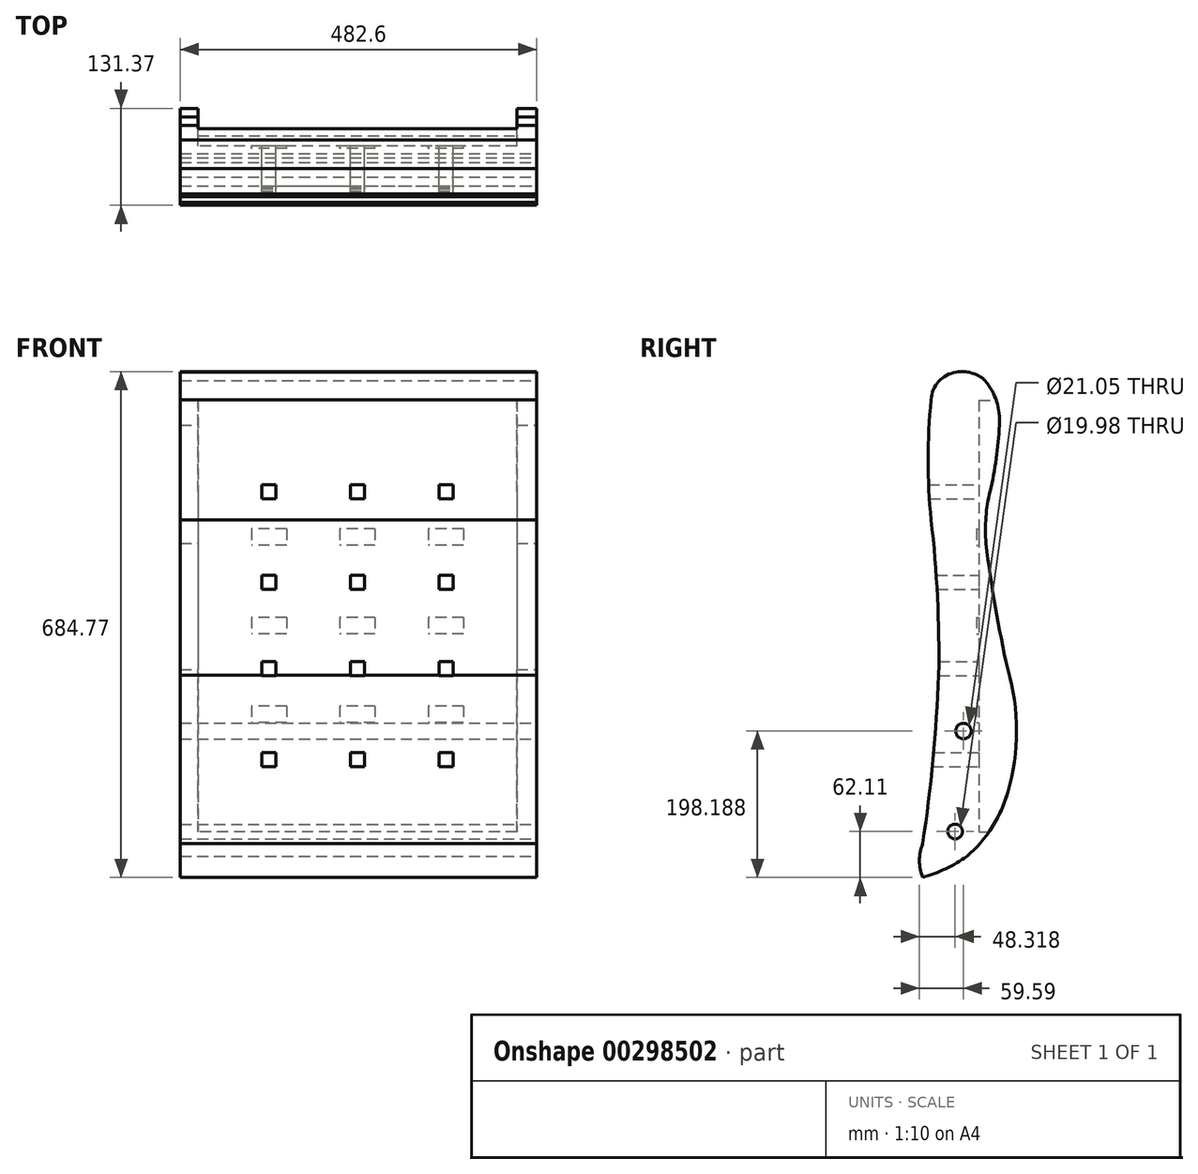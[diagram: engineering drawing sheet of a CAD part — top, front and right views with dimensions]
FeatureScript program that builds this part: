
annotation { "Feature Type Name" : "Feature", "Feature Type Description" : "" }
export const myFeature = defineFeature(function(context is Context, id is Id, definition is map)
    precondition{}
    {
        {
            var Q0;
            Q0=qCreatedBy(makeId("Front.planeOp"),FACE);
            var sketch = newSketch(context, id + "F0", { "sketchPlane" : qUnion([Q0])});
            skLineSegment(sketch, "E0.top", {"start": v(-241.3, -349.25) * mm, "end": v(241.3, -349.25) * mm});
            skLineSegment(sketch, "E0.left", {"start": v(-241.3, 323.85) * mm, "end": v(-241.3, -349.25) * mm});
            skLineSegment(sketch, "E0.right", {"start": v(241.3, 323.85) * mm, "end": v(241.3, -349.25) * mm});
            skPoint(sketch, "E1", {"position": v(0, 0) * mm});
            skPoint(sketch, "E1.positionSnap0", {"position": v(-241.3, 0) * mm});
            skPoint(sketch, "E1.positionSnap1", {"position": v(0, 349.25) * mm});
            skArc(sketch, "E2", {"start": v(241.3, 323.85) * mm, "mid": v(0, 349.25) * mm, "end": v(-241.3, 323.85) * mm});
            skPoint(sketch, "E3.orphan", {"position": v(-241.3, 349.25) * mm});
            skPoint(sketch, "E4.orphan", {"position": v(241.3, 349.25) * mm});
            skSolve(sketch);
        }
        {
            var Q0;
            Q0=makeQuery(id+"F0.imprint","IMPRINT",FACE,{"disambiguationData":[TD([[makeQuery(id+"F0.imprint","IMPRINT",EDGE,{"derivedFrom":sQuery(id+"F0.wireOp",EDGE,"E0.top")}),1.0]])]});
            extrude(context, id + "F1", {"entities" : qUnion([Q0]), "depth" : 120.65 * mm});
        }
        {
            var Q0;
            Q0=makeQuery(id+"F1.opExtrude","SWEPT_FACE",FACE,{"disambiguationData":[OSD([sQuery(id+"F0.wireOp",EDGE,"E0.left")])]});
            var sketch = newSketch(context, id + "F2", { "sketchPlane" : qUnion([Q0])});
            skArc(sketch, "E5", {"start": v(0, -233.65) * mm, "mid": v(21.35, -281.15) * mm, "end": v(55.28, -320.65) * mm});
            skArc(sketch, "E6", {"start": v(0, -68.14) * mm, "mid": v(-11.67, -150.9) * mm, "end": v(0, -233.65) * mm});
            skArc(sketch, "E7", {"start": v(0, -68.14) * mm, "mid": v(17, 17.17) * mm, "end": v(29.6, 103.23) * mm});
            skArc(sketch, "E8", {"start": v(29.6, 103.23) * mm, "mid": v(29.63, 138.4) * mm, "end": v(24.18, 173.15) * mm});
            skArc(sketch, "E9", {"start": v(11.41, 262.84) * mm, "mid": v(15.69, 217.7) * mm, "end": v(24.18, 173.15) * mm});
            skArc(sketch, "E10", {"start": v(30.93, 323.38) * mm, "mid": v(15.23, 295.03) * mm, "end": v(11.41, 262.84) * mm});
            skArc(sketch, "E11", {"start": v(69.98, 334.7) * mm, "mid": v(49.09, 333.77) * mm, "end": v(30.93, 323.38) * mm});
            skArc(sketch, "E12", {"start": v(103.92, 297.53) * mm, "mid": v(93.59, 322.17) * mm, "end": v(69.98, 334.7) * mm});
            skArc(sketch, "E13", {"start": v(103.92, 134.9) * mm, "mid": v(108, 216.21) * mm, "end": v(103.92, 297.53) * mm});
            skArc(sketch, "E14", {"start": v(103.92, 134.9) * mm, "mid": v(95.3, 29.96) * mm, "end": v(93.63, -75.3) * mm});
            skArc(sketch, "E15", {"start": v(93.63, -75.3) * mm, "mid": v(101.35, -189.73) * mm, "end": v(115.32, -303.56) * mm});
            skArc(sketch, "E16", {"start": v(115.32, -349.25) * mm, "mid": v(119.7, -326.4) * mm, "end": v(115.32, -303.56) * mm});
            skArc(sketch, "E17", {"start": v(55.28, -320.65) * mm, "mid": v(84.07, -337.54) * mm, "end": v(115.32, -349.25) * mm});
            skCircle(sketch, "E18", {"center": v(60.1, -151.06) * mm, "radius": 10.53 * mm});
            skCircle(sketch, "E19", {"center": v(71.38, -287.14) * mm, "radius": 9.99 * mm});
            skSolve(sketch);
        }
        {
            var Q0;
            {var subQ8=sQuery(id+"F2.wireOp",EDGE,"E5");Q0=makeQuery(id+"F2.imprint","IMPRINT",FACE,{"disambiguationData":[TD([[makeQuery(id+"F2.imprint","IMPRINT",EDGE,{"derivedFrom":subQ8}),1.0]])]});}
            var Q1;
            {var subQ0=sQuery(id+"F2.wireOp",EDGE,"E11");Q1=makeQuery(id+"F2.imprint","IMPRINT",FACE,{"disambiguationData":[TD([[makeQuery(id+"F2.imprint","IMPRINT",EDGE,{"derivedFrom":subQ0}),1.0]])]});}
            var Q2;
            {var subQ0=sQuery(id+"F2.wireOp",EDGE,"E6");Q2=makeQuery(id+"F2.imprint","IMPRINT",FACE,{"disambiguationData":[TD([[makeQuery(id+"F2.imprint","IMPRINT",EDGE,{"derivedFrom":subQ0}),1.0]])]});}
            extrude(context, id + "F3", {"entities" : qUnion([Q0, Q1, Q2]), "depth" : 482.6 * mm});
        }
        {
            var Q0;
            Q0=makeQuery(id+"F1.opExtrude","SWEPT_FACE",FACE,{"disambiguationData":[OSD([sQuery(id+"F0.wireOp",EDGE,"E0.right")])]});
            var sketch = newSketch(context, id + "F4", { "sketchPlane" : qUnion([Q0])});
            skLineSegment(sketch, "E20.bottom", {"start": v(-225.7, 393.7) * mm, "end": v(119.19, 393.7) * mm});
            skLineSegment(sketch, "E20.top", {"start": v(-225.7, -371) * mm, "end": v(119.19, -371) * mm});
            skLineSegment(sketch, "E20.left", {"start": v(-225.7, 393.7) * mm, "end": v(-225.7, -371) * mm});
            skLineSegment(sketch, "E20.right", {"start": v(119.19, 393.7) * mm, "end": v(119.19, -371) * mm});
            skSolve(sketch);
        }
        {
            var Q0;
            Q0=makeQuery(id+"F4.imprint","IMPRINT",FACE,{"disambiguationData":[TD([[makeQuery(id+"F4.imprint","IMPRINT",EDGE,{"derivedFrom":sQuery(id+"F4.wireOp",EDGE,"E20.bottom")}),-1.0]])]});
            var Q1;
            {var subQ0=sQuery(id+"F0.wireOp",EDGE,"E0.right");Q1=makeQuery(id+"F4.imprint","IMPRINT",FACE,{"disambiguationData":[TD([[makeQuery(id+"F4.imprint","IMPRINT",EDGE,{"derivedFrom":makeQuery(id+"F1.opExtrude","CAP_EDGE",EDGE,{"disambiguationData":[OSD([subQ0])],"isStart":true})}),-1.0]])]});}
            extrude(context, id + "F5", {"entities" : qUnion([Q0, Q1]), "operationType" : NewBodyOperationType.REMOVE, "oppositeDirection" : true, "depth" : 482.6 * mm});
        }
        {
            var Q0;
            Q0=makeQuery(id+"F3.opExtrude","CAP_EDGE",EDGE,{"disambiguationData":[OSD([sQuery(id+"F2.wireOp",EDGE,"E6")])],"isStart":false});
            cPoint(context, id + "F6", {"entities" : qUnion([Q0]), "parameter" : 0.5});
        }
        {
            var Q0;
            Q0=qCreatedBy(makeId("Front.planeOp"),FACE);
            var Q1;
            Q1 = qCreatedBy(id + "F6" ,VERTEX);
            cPlane(context, id + "F7", {"entities" : qUnion([Q0, Q1]), "cplaneType" : CPlaneType.PLANE_POINT, "offset" : 25.4 * mm, "width" : 152.4 * mm, "height" : 152.4 * mm});
        }
        {
            var Q0;
            Q0=qCreatedBy(id+"F7.planeOp",FACE);
            var sketch = newSketch(context, id + "F8", { "sketchPlane" : qUnion([Q0])});
            skLineSegment(sketch, "E21.bottom", {"start": v(-268.03, 296.48) * mm, "end": v(-699.83, 296.48) * mm});
            skLineSegment(sketch, "E21.top", {"start": v(-268.03, -287.72) * mm, "end": v(-699.83, -287.72) * mm});
            skLineSegment(sketch, "E21.left", {"start": v(-268.03, 296.48) * mm, "end": v(-268.03, -287.72) * mm});
            skLineSegment(sketch, "E21.right", {"start": v(-699.83, 296.48) * mm, "end": v(-699.83, -287.72) * mm});
            skPoint(sketch, "E22", {"position": v(-483.93, 296.48) * mm});
            skSolve(sketch);
        }
        {
            var Q0;
            Q0=makeQuery(id+"F8.imprint","IMPRINT",FACE,{"disambiguationData":[TD([[makeQuery(id+"F8.imprint","IMPRINT",EDGE,{"derivedFrom":sQuery(id+"F8.wireOp",EDGE,"E21.bottom")}),1.0]])]});
            extrude(context, id + "F9", {"entities" : qUnion([Q0]), "operationType" : NewBodyOperationType.REMOVE, "depth" : 50.8 * mm, "offsetDistance" : 25.4 * mm});
        }
        {
            var Q0;
            Q0=makeQuery(id+"F9.boolean.opBoolean","COPY",FACE,{"derivedFrom":makeQuery(id+"F9.opExtrude","CAP_FACE",FACE,{"disambiguationData":[OSD([sQuery(id+"F8.wireOp",EDGE,"E21.bottom"),sQuery(id+"F8.wireOp",EDGE,"E21.top"),sQuery(id+"F8.wireOp",EDGE,"E21.left"),sQuery(id+"F8.wireOp",EDGE,"E21.right")])],"isStart":false})});
            var sketch = newSketch(context, id + "F10", { "sketchPlane" : qUnion([Q0])});
            skLineSegment(sketch, "E23.bottom", {"start": v(340.26, -117.06) * mm, "end": v(387.89, -117.06) * mm});
            skLineSegment(sketch, "E23.top", {"start": v(340.26, -139.29) * mm, "end": v(387.89, -139.29) * mm});
            skLineSegment(sketch, "E23.left", {"start": v(340.26, -117.06) * mm, "end": v(340.26, -139.29) * mm});
            skLineSegment(sketch, "E23.right", {"start": v(387.89, -117.06) * mm, "end": v(387.89, -139.29) * mm});
            skLineSegment(sketch, "E24.bottom", {"start": v(579.98, 122.65) * mm, "end": v(627.6, 122.65) * mm});
            skLineSegment(sketch, "E24.top", {"start": v(579.98, 100.42) * mm, "end": v(627.6, 100.42) * mm});
            skLineSegment(sketch, "E24.left", {"start": v(579.98, 122.65) * mm, "end": v(579.98, 100.42) * mm});
            skLineSegment(sketch, "E24.right", {"start": v(627.6, 122.65) * mm, "end": v(627.6, 100.42) * mm});
            skLineSegment(sketch, "E25.bottom", {"start": v(340.26, 122.65) * mm, "end": v(387.89, 122.65) * mm});
            skLineSegment(sketch, "E25.top", {"start": v(340.26, 100.42) * mm, "end": v(387.89, 100.42) * mm});
            skLineSegment(sketch, "E25.left", {"start": v(340.26, 122.65) * mm, "end": v(340.26, 100.42) * mm});
            skLineSegment(sketch, "E25.right", {"start": v(387.89, 122.65) * mm, "end": v(387.89, 100.42) * mm});
            skLineSegment(sketch, "E26.bottom", {"start": v(460.12, 122.65) * mm, "end": v(507.75, 122.65) * mm});
            skLineSegment(sketch, "E26.top", {"start": v(460.12, 100.42) * mm, "end": v(507.75, 100.42) * mm});
            skLineSegment(sketch, "E26.left", {"start": v(460.12, 122.65) * mm, "end": v(460.12, 100.42) * mm});
            skLineSegment(sketch, "E26.right", {"start": v(507.75, 122.65) * mm, "end": v(507.75, 100.42) * mm});
            skLineSegment(sketch, "E27.bottom", {"start": v(460.12, 2.8) * mm, "end": v(507.75, 2.8) * mm});
            skLineSegment(sketch, "E27.top", {"start": v(460.12, -19.43) * mm, "end": v(507.75, -19.43) * mm});
            skLineSegment(sketch, "E27.left", {"start": v(460.12, 2.8) * mm, "end": v(460.12, -19.43) * mm});
            skLineSegment(sketch, "E27.right", {"start": v(507.75, 2.8) * mm, "end": v(507.75, -19.43) * mm});
            skLineSegment(sketch, "E28.bottom", {"start": v(579.98, 2.8) * mm, "end": v(627.6, 2.8) * mm});
            skLineSegment(sketch, "E28.top", {"start": v(579.98, -19.43) * mm, "end": v(627.6, -19.43) * mm});
            skLineSegment(sketch, "E28.left", {"start": v(579.98, 2.8) * mm, "end": v(579.98, -19.43) * mm});
            skLineSegment(sketch, "E28.right", {"start": v(627.6, 2.8) * mm, "end": v(627.6, -19.43) * mm});
            skLineSegment(sketch, "E29.bottom", {"start": v(340.26, 2.8) * mm, "end": v(387.89, 2.8) * mm});
            skLineSegment(sketch, "E29.top", {"start": v(340.26, -19.43) * mm, "end": v(387.89, -19.43) * mm});
            skLineSegment(sketch, "E29.left", {"start": v(340.26, 2.8) * mm, "end": v(340.26, -19.43) * mm});
            skLineSegment(sketch, "E29.right", {"start": v(387.89, 2.8) * mm, "end": v(387.89, -19.43) * mm});
            skLineSegment(sketch, "E30.bottom", {"start": v(579.98, -117.06) * mm, "end": v(627.6, -117.06) * mm});
            skLineSegment(sketch, "E30.top", {"start": v(579.98, -139.29) * mm, "end": v(627.6, -139.29) * mm});
            skLineSegment(sketch, "E30.left", {"start": v(579.98, -117.06) * mm, "end": v(579.98, -139.29) * mm});
            skLineSegment(sketch, "E30.right", {"start": v(627.6, -117.06) * mm, "end": v(627.6, -139.29) * mm});
            skLineSegment(sketch, "E31.bottom", {"start": v(460.12, -117.06) * mm, "end": v(507.75, -117.06) * mm});
            skLineSegment(sketch, "E31.top", {"start": v(460.12, -139.29) * mm, "end": v(507.75, -139.29) * mm});
            skLineSegment(sketch, "E31.left", {"start": v(460.12, -117.06) * mm, "end": v(460.12, -139.29) * mm});
            skLineSegment(sketch, "E31.right", {"start": v(507.75, -117.06) * mm, "end": v(507.75, -139.29) * mm});
            skLineSegment(sketch, "E32", {"start": v(268.03, 220.28) * mm, "end": v(699.83, 220.28) * mm});
            skLineSegment(sketch, "E33", {"start": v(268.03, -236.92) * mm, "end": v(699.83, -236.92) * mm});
            skLineSegment(sketch, "E34.bottom", {"start": v(474.4, -180.17) * mm, "end": v(493.46, -180.17) * mm});
            skLineSegment(sketch, "E34.top", {"start": v(474.4, -199.22) * mm, "end": v(493.46, -199.22) * mm});
            skLineSegment(sketch, "E34.left", {"start": v(474.4, -180.17) * mm, "end": v(474.4, -199.22) * mm});
            skLineSegment(sketch, "E34.right", {"start": v(493.46, -180.17) * mm, "end": v(493.46, -199.22) * mm});
            skLineSegment(sketch, "E35.bottom", {"start": v(474.4, -57.14) * mm, "end": v(493.46, -57.14) * mm});
            skLineSegment(sketch, "E35.top", {"start": v(474.4, -76.19) * mm, "end": v(493.46, -76.19) * mm});
            skLineSegment(sketch, "E35.left", {"start": v(474.4, -57.14) * mm, "end": v(474.4, -76.19) * mm});
            skLineSegment(sketch, "E35.right", {"start": v(493.46, -57.14) * mm, "end": v(493.46, -76.19) * mm});
            skLineSegment(sketch, "E36.bottom", {"start": v(594.26, -57.14) * mm, "end": v(613.31, -57.14) * mm});
            skLineSegment(sketch, "E36.top", {"start": v(594.26, -76.19) * mm, "end": v(613.31, -76.19) * mm});
            skLineSegment(sketch, "E36.left", {"start": v(594.26, -57.14) * mm, "end": v(594.26, -76.19) * mm});
            skLineSegment(sketch, "E36.right", {"start": v(613.31, -57.14) * mm, "end": v(613.31, -76.19) * mm});
            skLineSegment(sketch, "E37.bottom", {"start": v(354.55, -180.17) * mm, "end": v(373.6, -180.17) * mm});
            skLineSegment(sketch, "E37.top", {"start": v(354.55, -199.22) * mm, "end": v(373.6, -199.22) * mm});
            skLineSegment(sketch, "E37.left", {"start": v(354.55, -180.17) * mm, "end": v(354.55, -199.22) * mm});
            skLineSegment(sketch, "E37.right", {"start": v(373.6, -180.17) * mm, "end": v(373.6, -199.22) * mm});
            skLineSegment(sketch, "E38.bottom", {"start": v(594.26, -180.17) * mm, "end": v(613.31, -180.17) * mm});
            skLineSegment(sketch, "E38.top", {"start": v(594.26, -199.22) * mm, "end": v(613.31, -199.22) * mm});
            skLineSegment(sketch, "E38.left", {"start": v(594.26, -180.17) * mm, "end": v(594.26, -199.22) * mm});
            skLineSegment(sketch, "E38.right", {"start": v(613.31, -180.17) * mm, "end": v(613.31, -199.22) * mm});
            skLineSegment(sketch, "E39.bottom", {"start": v(354.55, -57.14) * mm, "end": v(373.6, -57.14) * mm});
            skLineSegment(sketch, "E39.top", {"start": v(354.55, -76.19) * mm, "end": v(373.6, -76.19) * mm});
            skLineSegment(sketch, "E39.left", {"start": v(354.55, -57.14) * mm, "end": v(354.55, -76.19) * mm});
            skLineSegment(sketch, "E39.right", {"start": v(373.6, -57.14) * mm, "end": v(373.6, -76.19) * mm});
            skLineSegment(sketch, "E40.bottom", {"start": v(594.26, 59.55) * mm, "end": v(613.31, 59.55) * mm});
            skLineSegment(sketch, "E40.top", {"start": v(594.26, 40.5) * mm, "end": v(613.31, 40.5) * mm});
            skLineSegment(sketch, "E40.left", {"start": v(594.26, 59.55) * mm, "end": v(594.26, 40.5) * mm});
            skLineSegment(sketch, "E40.right", {"start": v(613.31, 59.55) * mm, "end": v(613.31, 40.5) * mm});
            skLineSegment(sketch, "E41.bottom", {"start": v(474.4, 59.55) * mm, "end": v(493.46, 59.55) * mm});
            skLineSegment(sketch, "E41.top", {"start": v(474.4, 40.5) * mm, "end": v(493.46, 40.5) * mm});
            skLineSegment(sketch, "E41.left", {"start": v(474.4, 59.55) * mm, "end": v(474.4, 40.5) * mm});
            skLineSegment(sketch, "E41.right", {"start": v(493.46, 59.55) * mm, "end": v(493.46, 40.5) * mm});
            skLineSegment(sketch, "E42.bottom", {"start": v(354.55, 59.55) * mm, "end": v(373.6, 59.55) * mm});
            skLineSegment(sketch, "E42.top", {"start": v(354.55, 40.5) * mm, "end": v(373.6, 40.5) * mm});
            skLineSegment(sketch, "E42.left", {"start": v(354.55, 59.55) * mm, "end": v(354.55, 40.5) * mm});
            skLineSegment(sketch, "E42.right", {"start": v(373.6, 59.55) * mm, "end": v(373.6, 40.5) * mm});
            skPoint(sketch, "E43", {"position": v(364.08, 59.55) * mm});
            skPoint(sketch, "E44", {"position": v(364.08, 100.42) * mm});
            skPoint(sketch, "E45", {"position": v(483.93, 59.55) * mm});
            skPoint(sketch, "E46", {"position": v(483.93, 100.42) * mm});
            skPoint(sketch, "E47", {"position": v(603.79, 100.42) * mm});
            skPoint(sketch, "E48", {"position": v(603.79, 59.55) * mm});
            skPoint(sketch, "E49", {"position": v(354.55, 50.02) * mm});
            skPoint(sketch, "E50", {"position": v(354.55, -66.66) * mm});
            skLineSegment(sketch, "E51.bottom", {"start": v(474.4, 182.58) * mm, "end": v(493.46, 182.58) * mm});
            skLineSegment(sketch, "E51.top", {"start": v(474.4, 163.53) * mm, "end": v(493.46, 163.53) * mm});
            skLineSegment(sketch, "E51.left", {"start": v(474.4, 182.58) * mm, "end": v(474.4, 163.53) * mm});
            skLineSegment(sketch, "E51.right", {"start": v(493.46, 182.58) * mm, "end": v(493.46, 163.53) * mm});
            skLineSegment(sketch, "E52.bottom", {"start": v(354.55, 182.58) * mm, "end": v(373.6, 182.58) * mm});
            skLineSegment(sketch, "E52.top", {"start": v(354.55, 163.53) * mm, "end": v(373.6, 163.53) * mm});
            skLineSegment(sketch, "E52.left", {"start": v(354.55, 182.58) * mm, "end": v(354.55, 163.53) * mm});
            skLineSegment(sketch, "E52.right", {"start": v(373.6, 182.58) * mm, "end": v(373.6, 163.53) * mm});
            skLineSegment(sketch, "E53.bottom", {"start": v(594.26, 182.58) * mm, "end": v(613.31, 182.58) * mm});
            skLineSegment(sketch, "E53.top", {"start": v(594.26, 163.53) * mm, "end": v(613.31, 163.53) * mm});
            skLineSegment(sketch, "E53.left", {"start": v(594.26, 182.58) * mm, "end": v(594.26, 163.53) * mm});
            skLineSegment(sketch, "E53.right", {"start": v(613.31, 182.58) * mm, "end": v(613.31, 163.53) * mm});
            skPoint(sketch, "E54", {"position": v(373.6, 50.02) * mm});
            skSolve(sketch);
        }
        {
            var Q0;
            Q0=makeQuery(id+"F10.imprint","IMPRINT",FACE,{"disambiguationData":[TD([[makeQuery(id+"F10.imprint","IMPRINT",EDGE,{"derivedFrom":sQuery(id+"F10.wireOp",EDGE,"E52.bottom")}),-1.0]])]});
            var Q1;
            Q1=makeQuery(id+"F10.imprint","IMPRINT",FACE,{"disambiguationData":[TD([[makeQuery(id+"F10.imprint","IMPRINT",EDGE,{"derivedFrom":sQuery(id+"F10.wireOp",EDGE,"E51.bottom")}),-1.0]])]});
            var Q2;
            Q2=makeQuery(id+"F10.imprint","IMPRINT",FACE,{"disambiguationData":[TD([[makeQuery(id+"F10.imprint","IMPRINT",EDGE,{"derivedFrom":sQuery(id+"F10.wireOp",EDGE,"E53.bottom")}),-1.0]])]});
            var Q3;
            Q3=makeQuery(id+"F10.imprint","IMPRINT",FACE,{"disambiguationData":[TD([[makeQuery(id+"F10.imprint","IMPRINT",EDGE,{"derivedFrom":sQuery(id+"F10.wireOp",EDGE,"E42.bottom")}),-1.0]])]});
            var Q4;
            Q4=makeQuery(id+"F10.imprint","IMPRINT",FACE,{"disambiguationData":[TD([[makeQuery(id+"F10.imprint","IMPRINT",EDGE,{"derivedFrom":sQuery(id+"F10.wireOp",EDGE,"E41.bottom")}),-1.0]])]});
            var Q5;
            Q5=makeQuery(id+"F10.imprint","IMPRINT",FACE,{"disambiguationData":[TD([[makeQuery(id+"F10.imprint","IMPRINT",EDGE,{"derivedFrom":sQuery(id+"F10.wireOp",EDGE,"E40.bottom")}),-1.0]])]});
            var Q6;
            Q6=makeQuery(id+"F10.imprint","IMPRINT",FACE,{"disambiguationData":[TD([[makeQuery(id+"F10.imprint","IMPRINT",EDGE,{"derivedFrom":sQuery(id+"F10.wireOp",EDGE,"E36.bottom")}),-1.0]])]});
            var Q7;
            Q7=makeQuery(id+"F10.imprint","IMPRINT",FACE,{"disambiguationData":[TD([[makeQuery(id+"F10.imprint","IMPRINT",EDGE,{"derivedFrom":sQuery(id+"F10.wireOp",EDGE,"E35.bottom")}),-1.0]])]});
            var Q8;
            Q8=makeQuery(id+"F10.imprint","IMPRINT",FACE,{"disambiguationData":[TD([[makeQuery(id+"F10.imprint","IMPRINT",EDGE,{"derivedFrom":sQuery(id+"F10.wireOp",EDGE,"E39.bottom")}),-1.0]])]});
            var Q9;
            Q9=makeQuery(id+"F10.imprint","IMPRINT",FACE,{"disambiguationData":[TD([[makeQuery(id+"F10.imprint","IMPRINT",EDGE,{"derivedFrom":sQuery(id+"F10.wireOp",EDGE,"E37.bottom")}),-1.0]])]});
            var Q10;
            Q10=makeQuery(id+"F10.imprint","IMPRINT",FACE,{"disambiguationData":[TD([[makeQuery(id+"F10.imprint","IMPRINT",EDGE,{"derivedFrom":sQuery(id+"F10.wireOp",EDGE,"E34.bottom")}),-1.0]])]});
            var Q11;
            Q11=makeQuery(id+"F10.imprint","IMPRINT",FACE,{"disambiguationData":[TD([[makeQuery(id+"F10.imprint","IMPRINT",EDGE,{"derivedFrom":sQuery(id+"F10.wireOp",EDGE,"E38.bottom")}),-1.0]])]});
            extrude(context, id + "F11", {"entities" : qUnion([Q0, Q1, Q2, Q3, Q4, Q5, Q6, Q7, Q8, Q9, Q10, Q11]), "operationType" : NewBodyOperationType.REMOVE, "oppositeDirection" : true, "depth" : 95.25 * mm});
        }
        {
            var Q0;
            Q0=makeQuery(id+"F10.imprint","IMPRINT",FACE,{"disambiguationData":[TD([[makeQuery(id+"F10.imprint","IMPRINT",EDGE,{"derivedFrom":sQuery(id+"F10.wireOp",EDGE,"E25.bottom")}),-1.0]])]});
            var Q1;
            Q1=makeQuery(id+"F10.imprint","IMPRINT",FACE,{"disambiguationData":[TD([[makeQuery(id+"F10.imprint","IMPRINT",EDGE,{"derivedFrom":sQuery(id+"F10.wireOp",EDGE,"E26.bottom")}),-1.0]])]});
            var Q2;
            Q2=makeQuery(id+"F10.imprint","IMPRINT",FACE,{"disambiguationData":[TD([[makeQuery(id+"F10.imprint","IMPRINT",EDGE,{"derivedFrom":sQuery(id+"F10.wireOp",EDGE,"E24.bottom")}),-1.0]])]});
            var Q3;
            Q3=makeQuery(id+"F10.imprint","IMPRINT",FACE,{"disambiguationData":[TD([[makeQuery(id+"F10.imprint","IMPRINT",EDGE,{"derivedFrom":sQuery(id+"F10.wireOp",EDGE,"E29.bottom")}),-1.0]])]});
            var Q4;
            Q4=makeQuery(id+"F10.imprint","IMPRINT",FACE,{"disambiguationData":[TD([[makeQuery(id+"F10.imprint","IMPRINT",EDGE,{"derivedFrom":sQuery(id+"F10.wireOp",EDGE,"E27.bottom")}),-1.0]])]});
            var Q5;
            Q5=makeQuery(id+"F10.imprint","IMPRINT",FACE,{"disambiguationData":[TD([[makeQuery(id+"F10.imprint","IMPRINT",EDGE,{"derivedFrom":sQuery(id+"F10.wireOp",EDGE,"E28.bottom")}),-1.0]])]});
            var Q6;
            Q6=makeQuery(id+"F10.imprint","IMPRINT",FACE,{"disambiguationData":[TD([[makeQuery(id+"F10.imprint","IMPRINT",EDGE,{"derivedFrom":sQuery(id+"F10.wireOp",EDGE,"E30.bottom")}),-1.0]])]});
            var Q7;
            Q7=makeQuery(id+"F10.imprint","IMPRINT",FACE,{"disambiguationData":[TD([[makeQuery(id+"F10.imprint","IMPRINT",EDGE,{"derivedFrom":sQuery(id+"F10.wireOp",EDGE,"E31.bottom")}),-1.0]])]});
            var Q8;
            Q8=makeQuery(id+"F10.imprint","IMPRINT",FACE,{"disambiguationData":[TD([[makeQuery(id+"F10.imprint","IMPRINT",EDGE,{"derivedFrom":sQuery(id+"F10.wireOp",EDGE,"E23.bottom")}),-1.0]])]});
            extrude(context, id + "F12", {"entities" : qUnion([Q0, Q1, Q2, Q3, Q4, Q5, Q6, Q7, Q8]), "operationType" : NewBodyOperationType.REMOVE, "oppositeDirection" : true, "depth" : 3.17 * mm});
        }
    });
